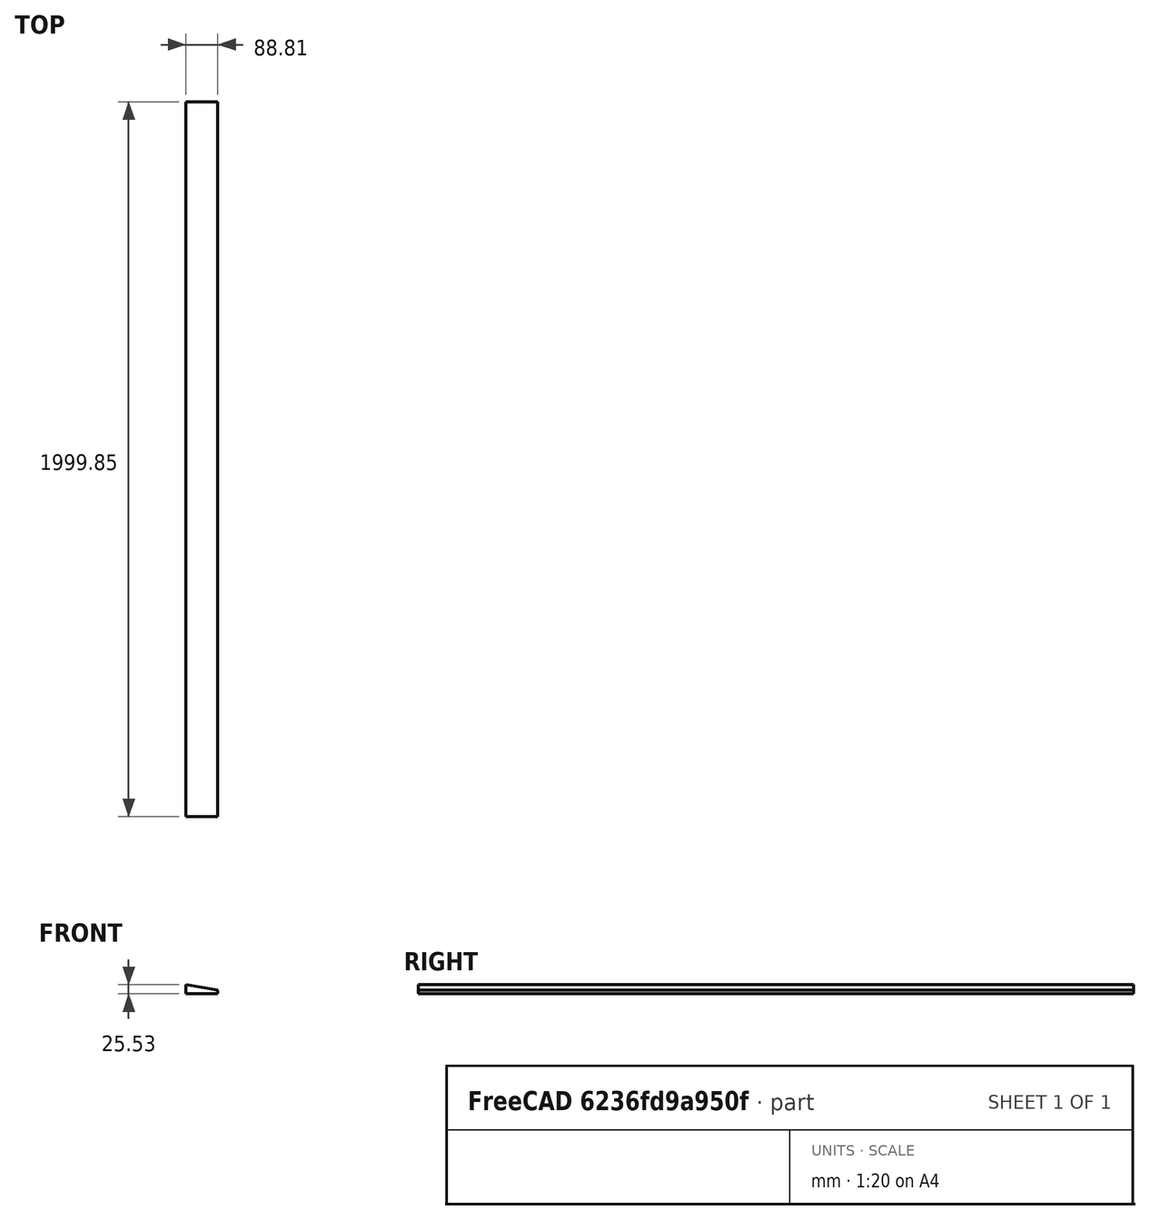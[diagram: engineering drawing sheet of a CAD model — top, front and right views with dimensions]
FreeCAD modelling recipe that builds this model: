
FCSTD DOCUMENT  (FreeCAD 0.18R15656 (Git))
Label: material tag test
License: All rights reserved
LicenseURL: http://en.wikipedia.org/wiki/All_rights_reserved
objects: App::MaterialObjectPython×146, Part::Part2DObjectPython×1, Part::FeaturePython×1, App::DocumentObjectGroupPython×1
note: 2 computed .brp shape members not serialized (recipe doc carries the construction recipe); baked Part::Feature solids carry a one-line shape summary decoded from their .brp

FEATURE [Part::Part2DObjectPython] Wire169002067078009  # Draft 2D object (typed FeaturePython)
  ChamferSize = 0
  Closed = true
  End = (15707.9,-1052.89,36542)
  FilletRadius = 0
  Length = 215.059
  MakeFace = true
  Placement = pos=(15619.1,-1052.89,36556.8) rot=(1,0,0;1.5708rad)
  Points = (4) [(0,0,0),(0,-25.5321,0),(88.8107,-25.5321,0),(88.8103,-14.8612,0)]
  Start = (15619.1,-1052.89,36556.8)
  Subdivisions = 0
FEATURE [App::MaterialObjectPython] Material  label="WOOD BLOCKING AS REQUIRED"  # material (typed FeaturePython)
  Material = Color=(0.6509803921568628, 0.48627450980392156, 0.3333333333333333),DiffuseColor=(0.6509804129600525, 0.48627451062202454, 0.3333333432674408),+3 more (map truncated)
  Transparency = 0
FEATURE [App::MaterialObjectPython] Material001  label="TREATED PLYWOOD SHEET"  # material (typed FeaturePython)
  Material = Color=(0.5019607843137255, 0.5019607843137255, 0.5019607843137255),DiffuseColor=(0.550000011920929, 0.6299999952316284, 0.41999998688697815),+3 more (map truncated)
  Transparency = 0
FEATURE [App::MaterialObjectPython] Material002  label="7/8" SMOOTH TROWEL EXTERIOR STUCCO OVER (2) LAYERS OF ORGANIC FELT"  # material (typed FeaturePython)
  Material = Color=(1.0, 1.0, 1.0); DiffuseColor=(1.0, 1.0, 1.0); Name=7/8" SMOOTH TROWEL EXTERIOR STUCCO; Transparency=0; ViewColor=(1.0, 1.0, 1.0)
  Transparency = 0
FEATURE [App::MaterialObjectPython] Material003  label="16 GA. COPPER SOFFIT DRIP SCREED"  # material (typed FeaturePython)
  Material = Color=(0.5019607843137255, 0.5019607843137255, 0.5019607843137255),DiffuseColor=(1.0, 0.8500000238418579, 0.0),Name=16 GA. COPPER SOFFIT DRIP SCREED,+2 more (map truncated)
  Transparency = 0
FEATURE [App::MaterialObjectPython] Material004  label="2 LAYERS NO. 30 ASTM D226 ASPHALT SATURATED ORGANIC FELT"  # material (typed FeaturePython)
  Material = Color=(0.5019607843137255, 0.5019607843137255, 0.5019607843137255),DiffuseColor=(0.18000000715255737, 0.6700000166893005, 0.0),+3 more (map truncated)
  Transparency = 0
FEATURE [App::MaterialObjectPython] Material005  label="STRUCTURAL MEMBER (SEE DWGS)"  # material (typed FeaturePython)
  Material = Color=(0.8392156862745098, 0.6980392156862745, 0.6196078431372549),DiffuseColor=(0.8392156958580017, 0.6980392336845398, 0.6196078658103943),+3 more (map truncated)
  Transparency = 0
FEATURE [App::MaterialObjectPython] Material006  label="CORNER BEAD"  # material (typed FeaturePython)
  Material = Color=(1.0, 0.9450980392156862, 0.0); DiffuseColor=(1.0, 0.9450980424880981, 0.0); Name=CORNER BEAD; Transparency=0; ViewColor=(1.0, 0.9450980392156862, 0.0)
  Transparency = 0
FEATURE [App::MaterialObjectPython] Material007  label="ALUMINIUM LOUVRE - TBD"  # material (typed FeaturePython)
  Material = Color=(0.5019607843137255, 0.5019607843137255, 0.5019607843137255),DiffuseColor=(0.36000001430511475, 0.41999998688697815, 0.47999998927116394),+3 more (map truncated)
  Transparency = 0
FEATURE [App::MaterialObjectPython] Material008  label="CDX PLYWOOD - SEE STRUCTURAL DWGS"  # material (typed FeaturePython)
  Material = Color=(0.5411764705882353, 0.36470588235294116, 0.19607843137254902),DiffuseColor=(0.5411764979362488, 0.364705890417099, 0.19607843458652496),+3 more (map truncated)
  Transparency = 0
FEATURE [App::MaterialObjectPython] Material009  label="WOOD FLOORING (SPEC TBD)"  # material (typed FeaturePython)
  Material = Color=(0.788235294117647, 0.6352941176470588, 0.49019607843137253),DiffuseColor=(0.7882353067398071, 0.6352941393852234, 0.4901960790157318),+3 more (map truncated)
  Transparency = 0
FEATURE [App::MaterialObjectPython] Material010  label="ALUMINIUM WINDOW - SEE ELEVATIONS FOR OPERATION"  # material (typed FeaturePython)
  Material = Color=(0.5019607843137255, 0.5019607843137255, 0.5019607843137255),DiffuseColor=(0.501960813999176, 0.501960813999176, 0.501960813999176),+3 more (map truncated)
  Transparency = 0
FEATURE [App::MaterialObjectPython] Material011  label="1" INSULATED GLAZING"  # material (typed FeaturePython)
  Material = Color=(0.5725490196078431, 0.7803921568627451, 0.8313725490196079),DiffuseColor=(0.572549045085907, 0.7803921699523926, 0.8313725590705872),+3 more (map truncated)
  Transparency = 75
FEATURE [App::MaterialObjectPython] Material012  label="SILL MATERIAL TBD"  # material (typed FeaturePython)
  Material = Color=(0.6901960784313725, 0.5254901960784314, 0.37254901960784315),DiffuseColor=(0.6200000047683716, 0.4399999976158142, 0.27000001072883606),+3 more (map truncated)
  Transparency = 0
FEATURE [App::MaterialObjectPython] Material013  label="5/8" GYPSUM BOARD"  # material (typed FeaturePython)
  Material = Color=(1.0, 1.0, 1.0); DiffuseColor=(1.0, 1.0, 1.0); Name=1/2" GYPSUM LAYER; Transparency=0; ViewColor=(1.0, 1.0, 1.0)
  Transparency = 0
FEATURE [App::MaterialObjectPython] Material014  label="BASE PER SCHEDULE"  # material (typed FeaturePython)
  Material = Color=(0.5803921568627451, 0.403921568627451, 0.23529411764705882),DiffuseColor=(0.5803921818733215, 0.40392157435417175, 0.23529411852359772),+3 more (map truncated)
  Transparency = 0
FEATURE [App::MaterialObjectPython] Material015  label="WOOD FRAMING (SEE STRUCT DWGS)"  # material (typed FeaturePython)
  Material = Color=(0.8784313725490196, 0.7372549019607844, 0.6588235294117647),DiffuseColor=(0.8784313797950745, 0.7372549176216125, 0.658823549747467),+3 more (map truncated)
  Transparency = 0
FEATURE [App::MaterialObjectPython] Material016  label="BATT INSULATION (U-FACTOR = 0.065 MIN.) OVER CLASS II VAPOR RETARDER (TOWARDS INTERIOR)"  # material (typed FeaturePython)
  Material = Color=(0.9647058823529412, 0.9490196078431372, 0.6274509803921569),DiffuseColor=(0.9647058844566345, 0.9490196108818054, 0.6274510025978088),+3 more (map truncated)
  Transparency = 0
FEATURE [App::MaterialObjectPython] Material017  label="16 GA. COPPER VENTED T REVEAL BEAD"  # material (typed FeaturePython)
  Material = Color=(1.0, 0.8901960784313725, 0.0392156862745098),DiffuseColor=(1.0, 0.8901960849761963, 0.03921568766236305),+3 more (map truncated)
  Transparency = 0
FEATURE [App::MaterialObjectPython] Material018  label="STRUCTURAL MEMBER (SEE STRUCTURAL DWGS)"  # material (typed FeaturePython)
  Material = Color=(0.6901960784313725, 0.5254901960784314, 0.37254901960784315),DiffuseColor=(0.6901960968971252, 0.5254902243614197, 0.37254902720451355),+3 more (map truncated)
  Transparency = 0
FEATURE [App::MaterialObjectPython] Material019  label="16GA. COPPER BRAKE METAL FLASHING"  # material (typed FeaturePython)
  Material = Color=(0.5019607843137255, 0.5019607843137255, 0.5019607843137255),DiffuseColor=(0.501960813999176, 0.501960813999176, 0.501960813999176),+3 more (map truncated)
  Transparency = 0
FEATURE [App::MaterialObjectPython] Material020  label="STANDING SEAM METAL ROOF FOLLOW MANU. RECOMMENDED EDGE/TRANSITION DETAILS"  # material (typed FeaturePython)
  Material = Color=(0.5019607843137255, 0.5019607843137255, 0.5019607843137255),DiffuseColor=(0.501960813999176, 0.501960813999176, 0.501960813999176),+3 more (map truncated)
  Transparency = 0
FEATURE [App::MaterialObjectPython] Material021  label="16 GA. COPPER WEEP SCREED W/ MIN 3 1/2" ATTACHMENT FLANGE - LAP UNDERLAYMENT OVER WEED SCREED"  # material (typed FeaturePython)
  Material = Color=(1.0, 0.9294117647058824, 0.0784313725490196),DiffuseColor=(1.0, 0.929411768913269, 0.0784313753247261),+3 more (map truncated)
  Transparency = 0
FEATURE [App::MaterialObjectPython] Material022  label="SEALANT"  # material (typed FeaturePython)
  Material = Color=(0.5568627450980392, 0.8823529411764706, 0.5803921568627451),DiffuseColor=(0.5568627715110779, 0.8823529481887817, 0.5803921818733215),+3 more (map truncated)
  Transparency = 0
FEATURE [App::MaterialObjectPython] Material023  label="CONCRETE EXPANSION JOINT - MINERAL FIBER"  # material (typed FeaturePython)
  Material = Color=(0.3215686274509804, 0.796078431372549, 0.10980392156862745),DiffuseColor=(0.32156863808631897, 0.7960784435272217, 0.10980392247438431),+3 more (map truncated)
  Transparency = 0
FEATURE [App::MaterialObjectPython] Material024  label="4" CONCRETE SLAB - SEE CIVIL DWGS"  # material (typed FeaturePython)
  Material = Color=(0.5019607843137255, 0.5019607843137255, 0.5019607843137255),DiffuseColor=(0.501960813999176, 0.501960813999176, 0.501960813999176),+3 more (map truncated)
  Transparency = 0
FEATURE [App::MaterialObjectPython] Material025  label="2" SAND LAYER"  # material (typed FeaturePython)
  Material = Color=(0.9372549019607843, 0.807843137254902, 0.6),DiffuseColor=(0.9372549057006836, 0.8078431487083435, 0.6000000238418579),Name=2" SAND LAYER,+2 more (map truncated)
  Transparency = 0
FEATURE [App::MaterialObjectPython] Material026  label="4" MIN. CRUSHED GRAVEL (NO FINES)"  # material (typed FeaturePython)
  Material = Color=(0.5686274509803921, 0.6352941176470588, 0.7372549019607844),DiffuseColor=(0.5686274766921997, 0.6352941393852234, 0.7372549176216125),+3 more (map truncated)
  Transparency = 0
FEATURE [App::MaterialObjectPython] Material027  label="CONCRETE SLAB W/ GRADE BEAM (SEE STRUCT DWGS)"  # material (typed FeaturePython)
  Material = Color=(0.5019607843137255, 0.5019607843137255, 0.5019607843137255),DiffuseColor=(0.501960813999176, 0.501960813999176, 0.501960813999176),+3 more (map truncated)
  Transparency = 0
FEATURE [App::MaterialObjectPython] Material028  label="FLEETWOOD SERIES 250-T-04 FIXED UNIT WINDOW FRAME"  # material (typed FeaturePython)
  Material = Color=(0.5019607843137255, 0.5019607843137255, 0.5019607843137255),DiffuseColor=(0.501960813999176, 0.501960813999176, 0.501960813999176),+3 more (map truncated)
  Transparency = 0
FEATURE [App::MaterialObjectPython] Material030  label="FLEETWOOD SERIES 250-T-01 CASEMENT WINDOW FRAME"  # material (typed FeaturePython)
  Material = Color=(0.5019607843137255, 0.5019607843137255, 0.5019607843137255),DiffuseColor=(0.501960813999176, 0.501960813999176, 0.501960813999176),+3 more (map truncated)
  Transparency = 0
FEATURE [App::MaterialObjectPython] Material031  label="WHITE OAK OVER BUILDING WRAP"  # material (typed FeaturePython)
  Material = Color=(0.5803921568627451, 0.403921568627451, 0.23529411764705882),DiffuseColor=(0.5803921818733215, 0.40392157435417175, 0.23529411852359772),+3 more (map truncated)
  Transparency = 0
FEATURE [App::MaterialObjectPython] Material032  label="ZEE CLOSURE TRIM"  # material (typed FeaturePython)
  Material = Color=(0.5019607843137255, 0.5019607843137255, 0.5019607843137255),DiffuseColor=(0.501960813999176, 0.501960813999176, 0.501960813999176),+3 more (map truncated)
  Transparency = 0
FEATURE [App::MaterialObjectPython] Material033  label="HIGH EAVE FLASHING"  # material (typed FeaturePython)
  Material = Color=(0.5019607843137255, 0.5019607843137255, 0.5019607843137255),DiffuseColor=(0.501960813999176, 0.501960813999176, 0.501960813999176),+3 more (map truncated)
  Transparency = 0
FEATURE [App::MaterialObjectPython] Material034  label="TRIM CLEAT"  # material (typed FeaturePython)
  Material = Color=(0.5019607843137255, 0.5019607843137255, 0.5019607843137255),DiffuseColor=(1.0, 0.9100000262260437, 0.019999999552965164),Name=TRIM CLEAT,+2 more (map truncated)
  Transparency = 0
FEATURE [App::MaterialObjectPython] Material035  label="SEALANT AND BACKROD WHERE NECESSARY"  # material (typed FeaturePython)
  Material = Color=(0.6313725490196078, 0.8156862745098039, 0.30196078431372547),DiffuseColor=(0.6313725709915161, 0.8156862854957581, 0.3019607961177826),+3 more (map truncated)
  Transparency = 0
FEATURE [App::MaterialObjectPython] Material036  label="CONT. SEAMLESS 16 GA COPPER BRAKE METAL GUTTER"  # material (typed FeaturePython)
  Material = Color=(0.5019607843137255, 0.5019607843137255, 0.5019607843137255),DiffuseColor=(0.501960813999176, 0.501960813999176, 0.501960813999176),+3 more (map truncated)
  Transparency = 0
FEATURE [App::MaterialObjectPython] Material037  label="METAL COPING"  # material (typed FeaturePython)
  Material = Color=(0.5019607843137255, 0.5019607843137255, 0.5019607843137255),DiffuseColor=(0.501960813999176, 0.501960813999176, 0.501960813999176),+3 more (map truncated)
  Transparency = 0
FEATURE [App::MaterialObjectPython] Material038  label="BITUMINOUS BUILT-UP ROOF MEMBRANE"  # material (typed FeaturePython)
  Material = Color=(0.13333333333333333, 0.5686274509803921, 0.0),DiffuseColor=(0.13333334028720856, 0.5686274766921997, 0.0),Name=BITUMINOUS BUILD,Transparency=0,+1 more (map truncated)
  Transparency = 0
FEATURE [App::MaterialObjectPython] Material039  label="GRAVEL BALLAST"  # material (typed FeaturePython)
  Material = Color=(0.5019607843137255, 0.5019607843137255, 0.5019607843137255),DiffuseColor=(0.501960813999176, 0.501960813999176, 0.501960813999176),+3 more (map truncated)
  Transparency = 0
FEATURE [App::MaterialObjectPython] Material040  label="BITUMINOUS MEMBRANE - TBD"  # material (typed FeaturePython)
  Material = Color=(0.5019607843137255, 0.5019607843137255, 0.5019607843137255),DiffuseColor=(0.0, 0.6700000166893005, 0.11999999731779099),+3 more (map truncated)
  Transparency = 0
FEATURE [App::MaterialObjectPython] Material041  label="ECO ROOT BARRIER"  # material (typed FeaturePython)
  Material = Color=(0.5294117647058824, 1.0, 0.00784313725490196),DiffuseColor=(0.529411792755127, 1.0, 0.007843137718737125),Name=NON-WOVEN ROOT BARRIER,+2 more (map truncated)
  Transparency = 0
FEATURE [App::MaterialObjectPython] Material043  label="CR LAURENCE ALUMINIUM B5S SERIES STANDARD SQUARE BASE SHOE FOR 1/2" TEMPERED GLASS - SEE STRUCT. DWGS"  # material (typed FeaturePython)
  Material = Color=(0.5019607843137255, 0.5019607843137255, 0.5019607843137255),DiffuseColor=(0.501960813999176, 0.501960813999176, 0.501960813999176),+3 more (map truncated)
  Transparency = 0
FEATURE [App::MaterialObjectPython] Material044  label="1/2" TEMPERED GLASS"  # material (typed FeaturePython)
  Material = Color=(0.5019607843137255, 0.5019607843137255, 0.5019607843137255),DiffuseColor=(0.25, 0.8199999928474426, 0.949999988079071),Name=GLASS RAILING TBD,+2 more (map truncated)
  Transparency = 75
FEATURE [App::MaterialObjectPython] Material045  label="FIXATION SYSTEM FOR GLASS RAILING AS NEEDED"  # material (typed FeaturePython)
  Material = Color=(0.5019607843137255, 0.5019607843137255, 0.5019607843137255),DiffuseColor=(0.501960813999176, 0.501960813999176, 0.501960813999176),+3 more (map truncated)
  Transparency = 0
FEATURE [App::MaterialObjectPython] Material046  label="SUPPORT SYSTEM FOR TERRACE FLOOR"  # material (typed FeaturePython)
  Material = Color=(1.0, 0.9921568627450981, 0.0),DiffuseColor=(1.0, 0.9921568632125854, 0.0),Name=SUPPORT SYSTEM FOR TERRACE FLOOR,Transparency=0,+1 more (map truncated)
  Transparency = 0
FEATURE [App::MaterialObjectPython] Material047  label="TERRACE FLOORING TBD"  # material (typed FeaturePython)
  Material = Color=(0.5019607843137255, 0.5019607843137255, 0.5019607843137255),DiffuseColor=(0.501960813999176, 0.501960813999176, 0.501960813999176),+3 more (map truncated)
  Transparency = 0
FEATURE [App::MaterialObjectPython] Material048  label="GROUND SOIL"  # material (typed FeaturePython)
  Material = Color=(0.6666666666666666, 0.48627450980392156, 0.29411764705882354),DiffuseColor=(0.6666666865348816, 0.48627451062202454, 0.29411765933036804),+3 more (map truncated)
  Transparency = 0
FEATURE [App::MaterialObjectPython] Material049  label="STEEL STRUCTURE (SEE STRUCTURAL DWGS)"  # material (typed FeaturePython)
  Material = Color=(0.5019607843137255, 0.5019607843137255, 0.5019607843137255),DiffuseColor=(0.501960813999176, 0.501960813999176, 0.501960813999176),+3 more (map truncated)
  Transparency = 0
FEATURE [App::MaterialObjectPython] Material050  label="METALLIC GRAVEL RETAINER"  # material (typed FeaturePython)
  Material = Color=(0.5019607843137255, 0.5019607843137255, 0.5019607843137255),DiffuseColor=(0.501960813999176, 0.501960813999176, 0.501960813999176),+3 more (map truncated)
  Transparency = 0
FEATURE [App::MaterialObjectPython] Material051  label="L-SHAPED METAL TRIM"  # material (typed FeaturePython)
  Material = Color=(1.0, 0.9058823529411765, 0.0); DiffuseColor=(1.0, 0.9058823585510254, 0.0); Name=L-shaped metal trim; Transparency=0; ViewColor=(1.0, 0.9058823529411765, 0.0)
  Transparency = 0
FEATURE [App::MaterialObjectPython] Material052  label="2" STONE DECK TBD"  # material (typed FeaturePython)
  Material = Color=(0.7803921568627451, 0.7254901960784313, 0.6784313725490196),DiffuseColor=(0.7803921699523926, 0.7254902124404907, 0.6784313917160034),+3 more (map truncated)
  Transparency = 0
FEATURE [App::MaterialObjectPython] Material053  label="BUZON PEDESTAL"  # material (typed FeaturePython)
  Material = Color=(0.25882352941176473, 0.25882352941176473, 0.25882352941176473),DiffuseColor=(0.25882354378700256, 0.25882354378700256, 0.25882354378700256),+3 more (map truncated)
  Transparency = 0
FEATURE [App::MaterialObjectPython] Material055  label="4" CMU WALL"  # material (typed FeaturePython)
  Material = Color=(0.5019607843137255, 0.5019607843137255, 0.5019607843137255),DiffuseColor=(0.501960813999176, 0.501960813999176, 0.501960813999176),+3 more (map truncated)
  Transparency = 0
FEATURE [App::MaterialObjectPython] Material056  label="SPLIT FACE STONE"  # material (typed FeaturePython)
  Material = Color=(0.803921568627451, 0.7647058823529411, 0.7098039215686275),DiffuseColor=(0.8039215803146362, 0.7647058963775635, 0.7098039388656616),+3 more (map truncated)
  Transparency = 0
FEATURE [App::MaterialObjectPython] Material057  label="MORTAR BED"  # material (typed FeaturePython)
  Material = Color=(0.5019607843137255, 0.5019607843137255, 0.5019607843137255),DiffuseColor=(0.7300000190734863, 0.7300000190734863, 0.7300000190734863),+3 more (map truncated)
  Transparency = 0
FEATURE [App::MaterialObjectPython] Material058  label="3/4" DRAINAGE CELL"  # material (typed FeaturePython)
  Material = Color=(1.0, 0.9882352941176471, 0.0); DiffuseColor=(1.0, 0.9882352948188782, 0.0); Name=3/4" DRAINAGE CELL; Transparency=0; ViewColor=(1.0, 0.9882352941176471, 0.0)
  Transparency = 0
FEATURE [App::MaterialObjectPython] Material059  label="GEOTEXTILE FILTER FABRIC"  # material (typed FeaturePython)
  Material = Color=(0.996078431372549, 1.0, 0.5294117647058824),DiffuseColor=(0.9960784316062927, 1.0, 0.529411792755127),Name=GEOTEXTILE FILTER FABRIC,+2 more (map truncated)
  Transparency = 0
FEATURE [App::MaterialObjectPython] Material060  label="RECEIVER TRIM"  # material (typed FeaturePython)
  Material = Color=(1.0, 0.9803921568627451, 0.0); DiffuseColor=(1.0, 0.9803921580314636, 0.0); Name=RECEIVER TRIM; Transparency=0; ViewColor=(1.0, 0.9803921568627451, 0.0)
  Transparency = 0
FEATURE [App::MaterialObjectPython] Material061  label="ANGLE TRIM"  # material (typed FeaturePython)
  Material = Color=(0.9803921568627451, 1.0, 0.0); DiffuseColor=(0.9803921580314636, 1.0, 0.0); Name=ANGLE TRIM; Transparency=0; ViewColor=(0.9803921568627451, 1.0, 0.0)
  Transparency = 0
FEATURE [App::MaterialObjectPython] Material062  label="2X SLOPED SLEEPERS - SLOPE TO DRAINS"  # material (typed FeaturePython)
  Material = Color=(0.9176470588235294, 0.7764705882352941, 0.6980392156862745),DiffuseColor=(0.9176470637321472, 0.7764706015586853, 0.6980392336845398),+3 more (map truncated)
  Transparency = 0
FEATURE [App::MaterialObjectPython] Material064  label="WESTCOAT ALX UNDER TILE WATERPROOFING SYSTEM (FOLLOW MANUFACTURER'S INSTALLATION REQUIREMENTS)"  # material (typed FeaturePython)
  Material = Color=(0.10588235294117647, 0.9098039215686274, 0.0),DiffuseColor=(0.10588235408067703, 0.9098039269447327, 0.0),+3 more (map truncated)
  Transparency = 0
FEATURE [App::MaterialObjectPython] Material065  label="GASKETED WASHER FOR DRAINAGE"  # material (typed FeaturePython)
  Material = Color=(0.5019607843137255, 0.5019607843137255, 0.5019607843137255),DiffuseColor=(0.501960813999176, 0.501960813999176, 0.501960813999176),+3 more (map truncated)
  Transparency = 0
FEATURE [App::MaterialObjectPython] Material066  label="SHEET METAL "GRAVEL-STOP" SET IN FIRESONE MULTI-PURPOSE MB FLASHING CEMENT; PRIME FLANGE BEFORE STRIPPING"  # material (typed FeaturePython)
  Material = Color=(0.5019607843137255, 0.5019607843137255, 0.5019607843137255),DiffuseColor=(0.501960813999176, 0.501960813999176, 0.501960813999176),+3 more (map truncated)
  Transparency = 0
FEATURE [App::MaterialObjectPython] Material067  label="CONCRETE FOOTING - SEE STRUCTURAL DWGS"  # material (typed FeaturePython)
  Material = Color=(0.5019607843137255, 0.5019607843137255, 0.5019607843137255),DiffuseColor=(0.501960813999176, 0.501960813999176, 0.501960813999176),+3 more (map truncated)
  Transparency = 0
FEATURE [App::MaterialObjectPython] Material074  label="1/2" GYPSUM LAYER"  # material (typed FeaturePython)
  Material = Color=(1.0, 1.0, 1.0); DiffuseColor=(1.0, 0.0, 0.0); Name=1/2" GYPSUM LAYER; Transparency=0; ViewColor=(1.0, 1.0, 1.0)
  Transparency = 0
FEATURE [App::MaterialObjectPython] Material107  label="GRAVEL LAYER"  # material (typed FeaturePython)
  Material = Color=(0.5019607843137255, 0.5019607843137255, 0.5019607843137255),DiffuseColor=(0.501960813999176, 0.501960813999176, 0.501960813999176),+3 more (map truncated)
  Transparency = 0
FEATURE [App::MaterialObjectPython] Material108  label="IGTP, 2x BLOCKING TO STOP POLY INSULATION"  # material (typed FeaturePython)
  Material = Color=(0.6509803921568628, 0.48627450980392156, 0.3333333333333333),DiffuseColor=(0.6509804129600525, 0.48627451062202454, 0.3333333432674408),+3 more (map truncated)
  Transparency = 0
FEATURE [App::MaterialObjectPython] Material109  label="3" POLYURETHANE SPRAY FOAM UNDER ROOF SUBSTRATE"  # material (typed FeaturePython)
  Material = Color=(1.0, 1.0, 1.0),DiffuseColor=(0.7568627595901489, 0.8901960849761963, 0.9607843160629272),Name=7/8" SMOOTH TROWEL EXTERIOR STUCCO,+2 more (map truncated)
  Transparency = 0
FEATURE [App::MaterialObjectPython] Material042  label="WHITE OAK (SPEC T.B.D.) OVER BUILDING WRAP"  # material (typed FeaturePython)
  Material = Color=(0.5411764705882353, 0.36470588235294116, 0.19607843137254902),DiffuseColor=(1.0, 0.9529411792755127, 0.8274509906768799),+3 more (map truncated)
  Transparency = 0
FEATURE [App::MaterialObjectPython] Material113  label="SELF ADHERED MEMBRANE W/ END DAMS WHERE POSSIBLE"  # material (typed FeaturePython)
  Material = Color=(0.6509803921568628, 0.48627450980392156, 0.3333333333333333),DiffuseColor=(1.0, 1.0, 0.49803921580314636),Name=WOOD BLOCKING AS REQUIRED,+2 more (map truncated)
  Transparency = 0
FEATURE [App::MaterialObjectPython] Material112  label="ASPHALT SATURATED ORGANIC FELT @ ROOF"  # material (typed FeaturePython)
  Material = Color=(0.6509803921568628, 0.48627450980392156, 0.3333333333333333),DiffuseColor=(0.3333333432674408, 0.6666666865348816, 0.49803921580314636),+3 more (map truncated)
  Transparency = 0
FEATURE [App::MaterialObjectPython] Material111  label="1X WOOD TRIM AS REQUIRED"  # material (typed FeaturePython)
  Material = Color=(0.6509803921568628, 0.48627450980392156, 0.3333333333333333),DiffuseColor=(0.6509804129600525, 0.48627451062202454, 0.3333333432674408),+3 more (map truncated)
  Transparency = 0
FEATURE [App::MaterialObjectPython] Material110  label="2X BLOCKING AS REQUIRED"  # material (typed FeaturePython)
  Material = Color=(0.6509803921568628, 0.48627450980392156, 0.3333333333333333),DiffuseColor=(0.6509804129600525, 0.48627451062202454, 0.3333333432674408),+3 more (map truncated)
  Transparency = 0
FEATURE [App::MaterialObjectPython] Material114  label="GRAVEL STOP REQUIRED WITH GRAVEL SURFACE SYSTEMS"  # material (typed FeaturePython)
  Material = Color=(1.0, 1.0, 0.4980392156862745),DiffuseColor=(0.6666666865348816, 0.6666666865348816, 0.49803921580314636),+3 more (map truncated)
  Transparency = 0
FEATURE [App::MaterialObjectPython] Material115  label="MODIFIED BITUMEN GRANULE SURFACED CAP SHEET"  # material (typed FeaturePython)
  Description = This is a not defined material
  Material = AuthorAndLicense=(c) 2015 Przemo Firszt (CC-BY 3.0),CardName=Standard Not Defined Material,+12 more (map truncated)
  Transparency = 0
FEATURE [App::MaterialObjectPython] Material116  label="INTERPLY"  # material (typed FeaturePython)
  Description = This is a not defined material
  Material = AuthorAndLicense=(c) 2015 Przemo Firszt (CC-BY 3.0),CardName=Standard Not Defined Material,+12 more (map truncated)
  Transparency = 0
FEATURE [App::MaterialObjectPython] Material117  label="1 3/4" STAINLESS STEEL RINGSHANK 5D COMMON NAILS @ 4" (101.6MM) O.C. FIRESTONE PROVIDED MAX., 1/2" STAGGERED"  # material (typed FeaturePython)
  Description = This is a not defined material
  Material = AuthorAndLicense=(c) 2015 Przemo Firszt (CC-BY 3.0),CardName=Standard Not Defined Material,Color=(1.0, 1.0, 1.0),Density=0 kg/m^3,+10 more (map truncated)
  Transparency = 0
FEATURE [App::MaterialObjectPython] Material118  label="CONTINUOUS CLEAT 1 3/4" STAINLESS STEEL RINGSHANK 5D COMMON NAILS @ 8" (203 MM) O.C. 3/4" FROM TOP OF FIRESTONE PROVIDED CLEAT."  # material (typed FeaturePython)
  Description = This is a not defined material
  Material = AuthorAndLicense=(c) 2015 Przemo Firszt (CC-BY 3.0),CardName=Standard Not Defined Material,Color=(1.0, 1.0, 1.0),Density=0 kg/m^3,+10 more (map truncated)
  Transparency = 0
FEATURE [App::MaterialObjectPython] Material119  label="FASTEN PLIES 6" (152 MM) O.C."  # material (typed FeaturePython)
  Description = This is a not defined material
  Material = AuthorAndLicense=(c) 2015 Przemo Firszt (CC-BY 3.0),CardName=Standard Not Defined Material,Color=(1.0, 1.0, 1.0),Density=0 kg/m^3,+10 more (map truncated)
  Transparency = 0
FEATURE [App::MaterialObjectPython] Material120  label="THREE PLY BUILT UP ROOF MEMBRANE"  # material (typed FeaturePython)
  Description = This is a not defined material
  Material = AuthorAndLicense=(c) 2015 Przemo Firszt (CC-BY 3.0),CardName=Standard Not Defined Material,+12 more (map truncated)
  Transparency = 0
FEATURE [App::MaterialObjectPython] Material054  label="COVER BOARD ( AS REQUIRED )"  # material (typed FeaturePython)
  Description = A standard construction wood
  Material = AuthorAndLicense=(c) 2015 Bernd Hahnebach (CC-BY 3.0),CardName=Standard Wood Material,Color=(1.0, 0.9019607843137255, 0.6509803921568628),+10 more (map truncated)
  ProductURL = http://en.wikipedia.org/wiki/Wood
  Transparency = 0
FEATURE [App::MaterialObjectPython] Material121  label="FIRESTONE INSULATION
(AS NEEDED)"  # material (typed FeaturePython)
  Material = Color=(0.3333333333333333, 0.3333333333333333, 0.0),DiffuseColor=(0.3333333432674408, 0.3333333432674408, 0.0),Name=FIRESTONE INSULATION\n(AS NEEDED),+2 more (map truncated)
  Transparency = 0
FEATURE [App::MaterialObjectPython] Material122  label="16 GA. COPPER VENTED SOFFIT DRIP SCREED"  # material (typed FeaturePython)
  Material = Color=(0.3333333333333333, 1.0, 0.4980392156862745),DiffuseColor=(0.3333333432674408, 1.0, 0.49803921580314636),+3 more (map truncated)
  Transparency = 0
FEATURE [App::MaterialObjectPython] Material123  label="5/8" GYP. BD."  # material (typed FeaturePython)
  Material = Color=(1.0, 1.0, 1.0); DiffuseColor=(0.8078431487083435, 1.0, 1.0); Name=5/8" GYP. BD.; Transparency=0; ViewColor=(1.0, 1.0, 1.0)
  Transparency = 0
FEATURE [App::MaterialObjectPython] Material124  label="TAPERED 2X SLEEPERS - SLOPED TO DRAIN"  # material (typed FeaturePython)
  Material = Color=(0.9176470588235294, 0.7764705882352941, 0.6980392156862745),DiffuseColor=(0.9176470637321472, 0.7764706015586853, 0.6980392336845398),+3 more (map truncated)
  Transparency = 0
FEATURE [App::MaterialObjectPython] Material125  label="BRAKE METAL FLASHING TO MATCH STOREFRONT"  # material (typed FeaturePython)
  Material = Color=(0.5019607843137255, 0.5019607843137255, 0.5019607843137255),DiffuseColor=(0.501960813999176, 0.501960813999176, 0.501960813999176),+3 more (map truncated)
  Transparency = 0
FEATURE [App::MaterialObjectPython] Material126  label="HARDWOOD TREAD SPECIES AND FINISH PER OWNER"  # material (typed FeaturePython)
  Material = Color=(0.7294117647058823, 0.5647058823529412, 0.4117647058823529),DiffuseColor=(0.729411780834198, 0.5647059082984924, 0.4117647111415863),+3 more (map truncated)
  Transparency = 0
FEATURE [App::MaterialObjectPython] Material127  label="SHAPED "T" TREAD SUPPORT PER STRUCTURAL, PAINTED"  # material (typed FeaturePython)
  Material = Color=(0.5019607843137255, 0.5019607843137255, 0.5019607843137255),DiffuseColor=(0.501960813999176, 0.501960813999176, 0.501960813999176),+3 more (map truncated)
  Transparency = 0
FEATURE [App::MaterialObjectPython] Material128  label="FLEETWOOD SERIES T3800 (SEE ELEVATIONS FOR OPERABILITY)"  # material (typed FeaturePython)
  Material = Color=(0.5019607843137255, 0.5019607843137255, 0.5019607843137255),DiffuseColor=(0.501960813999176, 0.501960813999176, 0.501960813999176),+3 more (map truncated)
  Transparency = 0
FEATURE [App::MaterialObjectPython] __4__TREATED_CDX_PLYWOOD_OVER_6_MIL_POLYETHYLENE_VAPOR_BARRIER  label="3/4" TREATED CDX PLYWOOD OVER 6 MIL POLYETHYLENE VAPOR BARRIER"  # material (typed FeaturePython)
  Material = DiffuseColor=(0.26274511218070984, 0.40392157435417175, 0.21960784494876862); Transparency=0
  Transparency = 0
FEATURE [App::MaterialObjectPython] Material130  label="ALUM. GLAZING CHANNEL"  # material (typed FeaturePython)
  Material = Color=(0.2196078431372549, 0.44313725490196076, 0.6666666666666666),DiffuseColor=(0.21960784494876862, 0.4431372582912445, 0.6666666865348816),+3 more (map truncated)
  Transparency = 0
FEATURE [App::MaterialObjectPython] Material131  label="1/2" INT. GLASS"  # material (typed FeaturePython)
  Material = Color=(0.5725490196078431, 0.7803921568627451, 0.8313725490196079),DiffuseColor=(0.572549045085907, 0.7803921699523926, 0.8313725590705872),+3 more (map truncated)
  Transparency = 75
FEATURE [App::MaterialObjectPython] Material132  label="ENGINEERED PANCAKE HEAD FASTENER (NOT BY AEP-SPAN) @ 12" O.C."  # material (typed FeaturePython)
  Description = This is a not defined material
  Material = AuthorAndLicense=(c) 2015 Przemo Firszt (CC-BY 3.0),CardName=Standard Not Defined Material,Color=(1.0, 1.0, 1.0),Density=0 kg/m^3,+10 more (map truncated)
  Transparency = 0
FEATURE [App::MaterialObjectPython] Material133  label="3/8" BEAD NON-SINKING BUTYL SEALANT"  # material (typed FeaturePython)
  Material = Color=(0.5490196078431373, 0.8156862745098039, 0.403921568627451),DiffuseColor=(0.5490196347236633, 0.8156862854957581, 0.40392157435417175),+3 more (map truncated)
  Transparency = 0
FEATURE [App::MaterialObjectPython] Material134  label="FIELD CUT AND BEND PANEL UP 1""  # material (typed FeaturePython)
  Material = Color=(0.179995422293431, 0.6699931334401464, 0.0),DiffuseColor=(0.17999541759490967, 0.6699931621551514, 0.0),Name=FIELD CUT AND BEND PANEL UP 1",+2 more (map truncated)
  Transparency = 0
FEATURE [App::MaterialObjectPython] Material135  label="REGLET TRIM001"  # material (typed FeaturePython)
  Material = Color=(0.5019607843137255, 0.5019607843137255, 0.5019607843137255),DiffuseColor=(0.501960813999176, 0.501960813999176, 0.501960813999176),+3 more (map truncated)
  Transparency = 0
FEATURE [App::MaterialObjectPython] Material136  label="RAKE WALL TRIM (RW212)"  # material (typed FeaturePython)
  Material = Color=(0.5019607843137255, 0.5019607843137255, 0.5019607843137255),DiffuseColor=(0.501960813999176, 0.501960813999176, 0.501960813999176),+3 more (map truncated)
  Transparency = 0
FEATURE [App::MaterialObjectPython] Material137  label="RECEIVER TRIM (PR138)"  # material (typed FeaturePython)
  Material = Color=(1.0, 0.9803921568627451, 0.0); DiffuseColor=(1.0, 0.9803921580314636, 0.0); Name=RECEIVER TRIM (PR138); Transparency=0; ViewColor=(1.0, 0.9803921568627451, 0.0)
  Transparency = 0
FEATURE [App::MaterialObjectPython] Material138  label="1/8" RIVETS @ 12" O.C."  # material (typed FeaturePython)
  Description = This is a not defined material
  Material = AuthorAndLicense=(c) 2015 Przemo Firszt (CC-BY 3.0),CardName=Standard Not Defined Material,Color=(1.0, 1.0, 1.0),Density=0 kg/m^3,+10 more (map truncated)
  Transparency = 0
FEATURE [App::MaterialObjectPython] Material139  label="SILL PAN"  # material (typed FeaturePython)
  Material = Color=(1.0, 1.0, 1.0); DiffuseColor=(1.0, 0.6666666865348816, 1.0); Name=SILL PAN; Transparency=0; ViewColor=(1.0, 1.0, 1.0)
  Transparency = 0
FEATURE [App::MaterialObjectPython] Material230  label="DOOR FRAME: TUBE STEEL PROFILE - METALIZED, PRIMED & PAINTED (COLOR PER ARCHITECT)"  # material (typed FeaturePython)
  Material = Color=(0.5019607843137255, 0.5019607843137255, 0.5019607843137255),DiffuseColor=(0.501960813999176, 0.501960813999176, 0.501960813999176),+3 more (map truncated)
  Transparency = 0
FEATURE [App::MaterialObjectPython] Material231  label="WOODEN LOUVERS (SPEC T. B. D.)"  # material (typed FeaturePython)
  Material = Color=(0.5803921568627451, 0.403921568627451, 0.23529411764705882),DiffuseColor=(0.5803921818733215, 0.40392157435417175, 0.23529411852359772),+3 more (map truncated)
  Transparency = 0
FEATURE [App::MaterialObjectPython] Material232  label="METALLIC PIVOT"  # material (typed FeaturePython)
  Material = Color=(0.5019607843137255, 0.5019607843137255, 0.5019607843137255),DiffuseColor=(0.501960813999176, 0.501960813999176, 0.501960813999176),+3 more (map truncated)
  Transparency = 0
FEATURE [App::MaterialObjectPython] Material233  label="16GA. COPPER BRAKE METAL FLASHING WITH END DAMS"  # material (typed FeaturePython)
  Material = Color=(0.5019607843137255, 0.5019607843137255, 0.5019607843137255),DiffuseColor=(0.501960813999176, 0.501960813999176, 0.501960813999176),+3 more (map truncated)
  Transparency = 0
FEATURE [App::MaterialObjectPython] Material234  label="BED OF SEALANT ABOVE AND BELOW FLASHING"  # material (typed FeaturePython)
  Material = Color=(0.2, 1.0, 0.0); DiffuseColor=(0.20000000298023224, 1.0, 0.0); Name=BED OF SEALANT ABOVE AND BELOW FLASHING; Transparency=0; ViewColor=(0.2, 1.0, 0.0)
  Transparency = 0
FEATURE [App::MaterialObjectPython] Material235  label="KOI POND / WATER"  # material (typed FeaturePython)
  Material = Color=(0.0, 0.4549019607843137, 1.0); DiffuseColor=(0.0, 0.45490196347236633, 1.0); Name=KOI POND / WATER; Transparency=75; ViewColor=(0.0, 0.4549019607843137, 1.0)
  Transparency = 75
FEATURE [App::MaterialObjectPython] Material236  label="BITUMINOUS MEMBRANE TBD"  # material (typed FeaturePython)
  Material = Color=(0.07450980392156863, 0.8549019607843137, 0.0),DiffuseColor=(0.07450980693101883, 0.8549019694328308, 0.0),Name=BITUMINOUS MEMBRANE TBD,+2 more (map truncated)
  Transparency = 0
FEATURE [App::MaterialObjectPython] Material237  label="METAL PROFILE"  # material (typed FeaturePython)
  Material = Color=(0.5019607843137255, 0.5019607843137255, 0.5019607843137255),DiffuseColor=(0.501960813999176, 0.501960813999176, 0.501960813999176),+3 more (map truncated)
  Transparency = 0
FEATURE [App::MaterialObjectPython] Material238  label="BRICK TBD"  # material (typed FeaturePython)
  Material = Color=(0.7137254901960784, 0.4196078431372549, 0.3254901960784314),DiffuseColor=(0.7137255072593689, 0.41960784792900085, 0.32549020648002625),+3 more (map truncated)
  Transparency = 0
FEATURE [App::MaterialObjectPython] Material239  label="FLEETWOOD SERIES 3070 (SEE ELEVATIONS FOR OPERABILITY)"  # material (typed FeaturePython)
  Material = Color=(0.5607843137254902, 0.5333333333333333, 0.5333333333333333),DiffuseColor=(0.5607843399047852, 0.5333333611488342, 0.5333333611488342),+3 more (map truncated)
  Transparency = 0
FEATURE [App::MaterialObjectPython] Material240  label="Material001"  # material (typed FeaturePython)
  Transparency = 0
FEATURE [App::MaterialObjectPython] Material241  label="RUBBER GASKET"  # material (typed FeaturePython)
  Material = Color=(0.27450980392156865, 0.27450980392156865, 0.27450980392156865),DiffuseColor=(0.27450981736183167, 0.27450981736183167, 0.27450981736183167),+3 more (map truncated)
  Transparency = 0
FEATURE [App::MaterialObjectPython] Material242  label="METAL PLATE"  # material (typed FeaturePython)
  Material = Color=(0.5019607843137255, 0.5019607843137255, 0.5019607843137255),DiffuseColor=(0.501960813999176, 0.501960813999176, 0.501960813999176),+3 more (map truncated)
  Transparency = 0
FEATURE [App::MaterialObjectPython] Material243  label="WELDED STEEL TABS FOR LOUVER ATTACHMENT"  # material (typed FeaturePython)
  Material = Color=(0.5019607843137255, 0.5019607843137255, 0.5019607843137255),DiffuseColor=(0.501960813999176, 0.501960813999176, 0.501960813999176),+3 more (map truncated)
  Transparency = 0
FEATURE [App::MaterialObjectPython] Material244  label="CONCRETE SLAB - SEE STRUCT. DWGS - SLOPE TOWARDS DRAINS"  # material (typed FeaturePython)
  Material = Color=(0.5019607843137255, 0.5019607843137255, 0.5019607843137255),DiffuseColor=(0.501960813999176, 0.501960813999176, 0.501960813999176),+3 more (map truncated)
  Transparency = 0
FEATURE [App::MaterialObjectPython] Material245  label="CONCRETE SLAB - SEE CIVIL MIN 2% SLOPE AWAY FROM BUILDING"  # material (typed FeaturePython)
  Material = Color=(0.5019607843137255, 0.5019607843137255, 0.5019607843137255),DiffuseColor=(0.501960813999176, 0.501960813999176, 0.501960813999176),+3 more (map truncated)
  Transparency = 0
FEATURE [App::MaterialObjectPython] Material246  label="TAPERED WOOD SLEEPERS - SLOPED TO DRAIN"  # material (typed FeaturePython)
  Material = Color=(0.9176470588235294, 0.7764705882352941, 0.6980392156862745),DiffuseColor=(0.9176470637321472, 0.7764706015586853, 0.6980392336845398),+3 more (map truncated)
  Transparency = 0
FEATURE [App::MaterialObjectPython] Material247  label="FASTEN INTO BLOCKING"  # material (typed FeaturePython)
  Description = This is a not defined material
  Material = AuthorAndLicense=(c) 2015 Przemo Firszt (CC-BY 3.0),CardName=Standard Not Defined Material,Color=(1.0, 1.0, 1.0),Density=0 kg/m^3,+10 more (map truncated)
  Transparency = 0
FEATURE [App::MaterialObjectPython] _6_GA__COPPER_SOFFIT_VENT___VERIFY_W__ARCHITECT_ON_LOCATION  label="16 GA. COPPER SOFFIT VENT - VERIFY W/ ARCHITECT ON LOCATION"  # material (typed FeaturePython)
  Material = DiffuseColor=(0.3333333432674408, 1.0, 0.49803921580314636); Transparency=0
  Transparency = 0
FEATURE [App::MaterialObjectPython] Material197  label="REQUIRED CANT STRIP"  # material (typed FeaturePython)
  Material = Color=(0.9176470588235294, 0.7764705882352941, 0.6980392156862745),DiffuseColor=(0.9176470637321472, 0.7764706015586853, 0.6980392336845398),+3 more (map truncated)
  Transparency = 0
FEATURE [App::MaterialObjectPython] Material248  label="RUBBER RING"  # material (typed FeaturePython)
  Material = Color=(0.25882352941176473, 0.25882352941176473, 0.25882352941176473),DiffuseColor=(0.25882354378700256, 0.25882354378700256, 0.25882354378700256),+3 more (map truncated)
  Transparency = 0
FEATURE [App::MaterialObjectPython] Material249  label="STEEL RAILING"  # material (typed FeaturePython)
  Material = Color=(0.5019607843137255, 0.5019607843137255, 0.5019607843137255),DiffuseColor=(0.501960813999176, 0.501960813999176, 0.501960813999176),+3 more (map truncated)
  Transparency = 0
FEATURE [App::MaterialObjectPython] Material250  label="BOLTS CONCEALED BY FLOOR FINISH"  # material (typed FeaturePython)
  Material = Color=(0.5019607843137255, 0.5019607843137255, 0.5019607843137255),DiffuseColor=(0.501960813999176, 0.501960813999176, 0.501960813999176),+3 more (map truncated)
  Transparency = 0
FEATURE [App::MaterialObjectPython] Material251  label="SILICON GASKET"  # material (typed FeaturePython)
  Material = Color=(0.23529411764705882, 0.788235294117647, 0.4823529411764706),DiffuseColor=(0.23529411852359772, 0.7882353067398071, 0.48235294222831726),+3 more (map truncated)
  Transparency = 0
FEATURE [App::MaterialObjectPython] Material252  label="WOOD VENEER AND EDGE DETAILING T. B. D."  # material (typed FeaturePython)
  Material = Color=(0.9098039215686274, 0.4980392156862745, 0.19215686274509805),DiffuseColor=(0.9098039269447327, 0.49803921580314636, 0.1921568661928177),+3 more (map truncated)
  Transparency = 0
FEATURE [App::MaterialObjectPython] Material253  label="BATT INSULATION AT CEILING/ROOF (R-FACTOR = R30 MIN) OVER CLASS II VAPOR RETARDER (TOWARD INTERIOR)"  # material (typed FeaturePython)
  Material = Color=(1.0, 0.9686274509803922, 0.48627450980392156),DiffuseColor=(1.0, 0.9686274528503418, 0.48627451062202454),+3 more (map truncated)
  Transparency = 0
FEATURE [App::MaterialObjectPython] Material254  label="TREATED WOOD BLOCKING"  # material (typed FeaturePython)
  Material = Color=(0.4470588235294118, 0.5294117647058824, 0.3176470588235294),DiffuseColor=(0.4470588266849518, 0.529411792755127, 0.3176470696926117),+3 more (map truncated)
  Transparency = 0
FEATURE [Part::FeaturePython] Structure668217386068  label="Structure668217191"  # Arch/BIM object (typed FeaturePython)
  Base = -> Wire169002067078009
  FaceMaker = 0
  Height = 1999.85
  HorizontalArea = 177607
  IfcAttributes = IfcUID=2Jq6hU9SSHwR9O200dNKHL
  IfcRole = 0
  Length = 0
  Material = -> Material254
  MoveWithHost = false
  Nodes = (2) [(15657.5,-1036.92,36524.9),(15657.5,-1036.92,34525)]
  NodesOffset = 0
  Normal = (0,1,0)
  PerimeterLength = 2177.47
  VerticalArea = 75615.9
  Width = 100
FEATURE [App::MaterialObjectPython] Material255  label="STAINLESS STEEL FLASHING"  # material (typed FeaturePython)
  Material = Color=(0.5019607843137255, 0.5019607843137255, 0.5019607843137255),DiffuseColor=(0.501960813999176, 0.501960813999176, 0.501960813999176),+3 more (map truncated)
  Transparency = 0
FEATURE [App::MaterialObjectPython] Material256  label="STEEL ANGLE (SIZE T. B. D.)"  # material (typed FeaturePython)
  Material = Color=(0.5019607843137255, 0.5019607843137255, 0.5019607843137255),DiffuseColor=(0.501960813999176, 0.501960813999176, 0.501960813999176),+3 more (map truncated)
  Transparency = 0
FEATURE [App::MaterialObjectPython] Material257  label="SILL SEALER"  # material (typed FeaturePython)
  Material = Color=(0.08235294117647059, 1.0, 0.0); DiffuseColor=(0.08235294371843338, 1.0, 0.0); Name=SILL SEALER; Transparency=0; ViewColor=(0.08235294117647059, 1.0, 0.0)
  Transparency = 0
FEATURE [App::MaterialObjectPython] Material258  label="TREATED 2x SILL PLATE - SEE STRUCT. DWGS FOR ATTACHMENT"  # material (typed FeaturePython)
  Material = Color=(0.5803921568627451, 0.403921568627451, 0.23529411764705882),DiffuseColor=(0.5803921818733215, 0.40392157435417175, 0.23529411852359772),+3 more (map truncated)
  Transparency = 0
FEATURE [App::MaterialObjectPython] Material259  label="ALUM STOREFRONT DOOR - 3200 FLEETWOOD"  # material (typed FeaturePython)
  Material = Color=(0.5019607843137255, 0.5019607843137255, 0.5019607843137255),DiffuseColor=(0.501960813999176, 0.501960813999176, 0.501960813999176),+3 more (map truncated)
  Transparency = 0
FEATURE [App::MaterialObjectPython] Material260  label="12 GAUGE STAINLESS STEEL FLASHING"  # material (typed FeaturePython)
  Material = Color=(0.0, 1.0, 0.0); DiffuseColor=(0.0, 1.0, 0.0); Name=12 GAUGE STAINLESS STEEL FLASHING; Transparency=0; ViewColor=(0.0, 1.0, 0.0)
  Transparency = 0
FEATURE [App::MaterialObjectPython] Material261  label="STONE/CONCRETE PAVERS T.B.D."  # material (typed FeaturePython)
  Material = Color=(0.5019607843137255, 0.5019607843137255, 0.5019607843137255),DiffuseColor=(0.501960813999176, 0.501960813999176, 0.501960813999176),+3 more (map truncated)
  Transparency = 0
FEATURE [App::MaterialObjectPython] Material262  label="LANDSCAPING STONE T.B.D."  # material (typed FeaturePython)
  Material = Color=(0.3607843137254902, 0.3607843137254902, 0.5411764705882353),DiffuseColor=(0.3607843220233917, 0.3607843220233917, 0.5411764979362488),+3 more (map truncated)
  Transparency = 0
FEATURE [App::MaterialObjectPython] Material263  label="1" BEDDING SAND"  # material (typed FeaturePython)
  Material = Color=(0.796078431372549, 0.8117647058823529, 0.5019607843137255),DiffuseColor=(0.7960784435272217, 0.8117647171020508, 0.501960813999176),+3 more (map truncated)
  Transparency = 0
FEATURE [App::MaterialObjectPython] Material264  label="GEOTEXTILE FABRIC - TURN UP @ EDGES"  # material (typed FeaturePython)
  Material = Color=(1.0, 0.8980392156862745, 0.792156862745098),DiffuseColor=(1.0, 0.8980392217636108, 0.7921568751335144),+3 more (map truncated)
  Transparency = 0
FEATURE [App::MaterialObjectPython] Material265  label="STEEL COLUMN CAP - SEE STRUCT. DWGS"  # material (typed FeaturePython)
  Material = Color=(0.7568627450980392, 0.7294117647058823, 0.6823529411764706),DiffuseColor=(0.7568627595901489, 0.729411780834198, 0.6823529601097107),+3 more (map truncated)
  Transparency = 0
FEATURE [App::MaterialObjectPython] Material266  label="STEEL COL. HSSS 4X4X1/2 SEE STRUCT. DWGS"  # material (typed FeaturePython)
  Material = Color=(0.7568627450980392, 0.7294117647058823, 0.6823529411764706),DiffuseColor=(0.7568627595901489, 0.729411780834198, 0.6823529601097107),+3 more (map truncated)
  Transparency = 0
FEATURE [App::MaterialObjectPython] Material267  label="STRUCTURAL STEEL - METALIZED AND PAINTED"  # material (typed FeaturePython)
  Material = Color=(0.7568627450980392, 0.7294117647058823, 0.6823529411764706),DiffuseColor=(0.7568627595901489, 0.729411780834198, 0.6823529601097107),+3 more (map truncated)
  Transparency = 0
FEATURE [App::MaterialObjectPython] Material268  label="CARRARA MARBLE"  # material (typed FeaturePython)
  Material = Color=(0.8705882352941177, 1.0, 0.8745098039215686),DiffuseColor=(0.8705882430076599, 1.0, 0.8745098114013672),Name=CARRARA MARBLE,Transparency=0,+1 more (map truncated)
  Transparency = 0
FEATURE [App::MaterialObjectPython] Material269  label="MILLWORK CONTRACTOR TO PROVIDE SUPPORT FOR STONE"  # material (typed FeaturePython)
  Material = Color=(0.5490196078431373, 0.4980392156862745, 0.3176470588235294),DiffuseColor=(0.5490196347236633, 0.49803921580314636, 0.3176470696926117),+3 more (map truncated)
  Transparency = 0
FEATURE [App::MaterialObjectPython] Material270  label="HEAVY DUTY STAINLESS STEEL HINGE (90 DEGREE ROTATION)"  # material (typed FeaturePython)
  Material = Color=(0.5019607843137255, 0.5019607843137255, 0.5019607843137255),DiffuseColor=(0.501960813999176, 0.501960813999176, 0.501960813999176),+3 more (map truncated)
  Transparency = 0
FEATURE [App::MaterialObjectPython] Material271  label="DRIP FLASHING"  # material (typed FeaturePython)
  Material = Color=(0.3333333333333333, 0.6666666666666666, 0.0),DiffuseColor=(0.3333333432674408, 0.6666666865348816, 0.0),Name=DRIP FLASHING,Transparency=0,+1 more (map truncated)
  Transparency = 0
FEATURE [App::MaterialObjectPython] Material272  label="WEATHERSTRIPPING"  # material (typed FeaturePython)
  Material = Color=(0.5019607843137255, 0.5019607843137255, 0.5019607843137255),DiffuseColor=(1.0, 0.666700005531311, 0.49799999594688416),+3 more (map truncated)
  Transparency = 0
FEATURE [App::MaterialObjectPython] Material273  label="ALUM. THRESHOLD"  # material (typed FeaturePython)
  Material = Color=(0.5019607843137255, 0.5019607843137255, 0.5019607843137255),DiffuseColor=(0.666700005531311, 1.0, 1.0),+3 more (map truncated)
  Transparency = 0
FEATURE [App::DocumentObjectGroupPython] MaterialContainer  label="Materials"  # scripted group (container) (typed FeaturePython)
  Group = -> [Material,Material001,Material002,Material003,Material004,Material005,Material006,Material007,Material008,Material009,Material010,Material011,Material012,Material013,Material014,Material015,Material016,Material017,Material018,Material019,Material020,Material021,Material022,Material023,Material024,Material025,Material026,Material027,Material028,Material030,Material031,Material032,Material033,+113 more]
